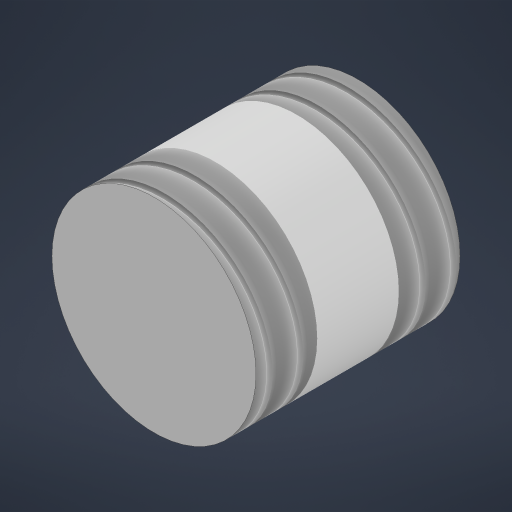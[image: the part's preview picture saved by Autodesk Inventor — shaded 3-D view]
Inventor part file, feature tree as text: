
AUTODESK INVENTOR PART (.ipt)
format: ipt  version: 2023 (Build 270158000, 158)  size: 204,800 bytes
history: native  units: mm
features: thread x2, extrude x1, sketch x1
ambient origin geometry x8: Origin, YZ Plane, XZ Plane, XY Plane, X Axis, Y Axis, Z Axis, Center Point
bodies: Solid1 (feature_tree)
feature tree (4):
  extrude  "Extrusion1"  Depth=10.0mm TaperAngle=0.0deg
  thread  "Thread1"  [1 undecoded]
  thread  "Thread2"  [1 undecoded]
  sketch  "Sketch1"  dims[d0=10.0mm d1=10.0mm d2=0.0mm d3=3.0mm d4=0.0mm d5=3.0mm d6=0.0mm]
note: 2 required parameter values undecoded (feature->parameter linkage not recoverable at this tier; creation-order binding heuristic only, values carry confidence <= 0.55)
